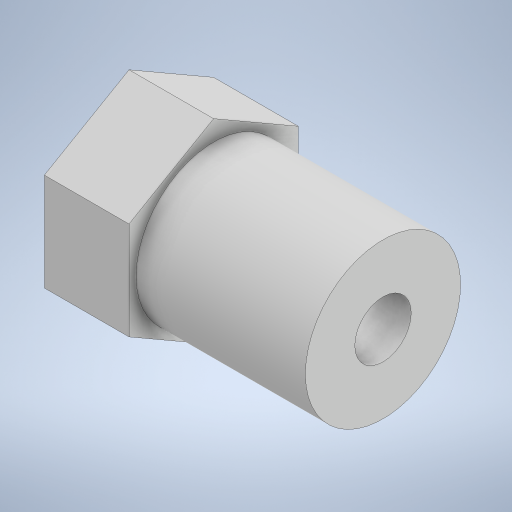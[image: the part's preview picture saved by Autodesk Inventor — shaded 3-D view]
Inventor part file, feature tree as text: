
AUTODESK INVENTOR PART (.ipt)
format: ipt  version: 2023 (Build 270158000, 158)  size: 232,960 bytes
history: native  units: mm
features: extrude x3, sketch x3
ambient origin geometry x8: Origin, YZ Plane, XZ Plane, XY Plane, X Axis, Y Axis, Z Axis, Center Point
bodies: Volumenkörper1 (feature_tree)
feature tree (6):
  extrude  "Extrusion1"  Depth=6.0mm TaperAngle=0.0deg
  extrude  "Extrusion2"  Depth=12.0mm TaperAngle=0.0deg
  extrude  "Extrusion3"  TaperAngle=0.0deg  [1 undecoded]
  sketch  "Skizze1"  dims[d0=12.0mm d1=6.0mm d2=0.0mm]
  sketch  "Skizze2"  dims[d3=11.0mm d4=12.0mm d5=0.0mm]
  sketch  "Skizze3"  dims[d6=4.0mm d7=0.0mm d8=0.0mm]
note: 1 required parameter value undecoded (feature->parameter linkage not recoverable at this tier; creation-order binding heuristic only, values carry confidence <= 0.55)
